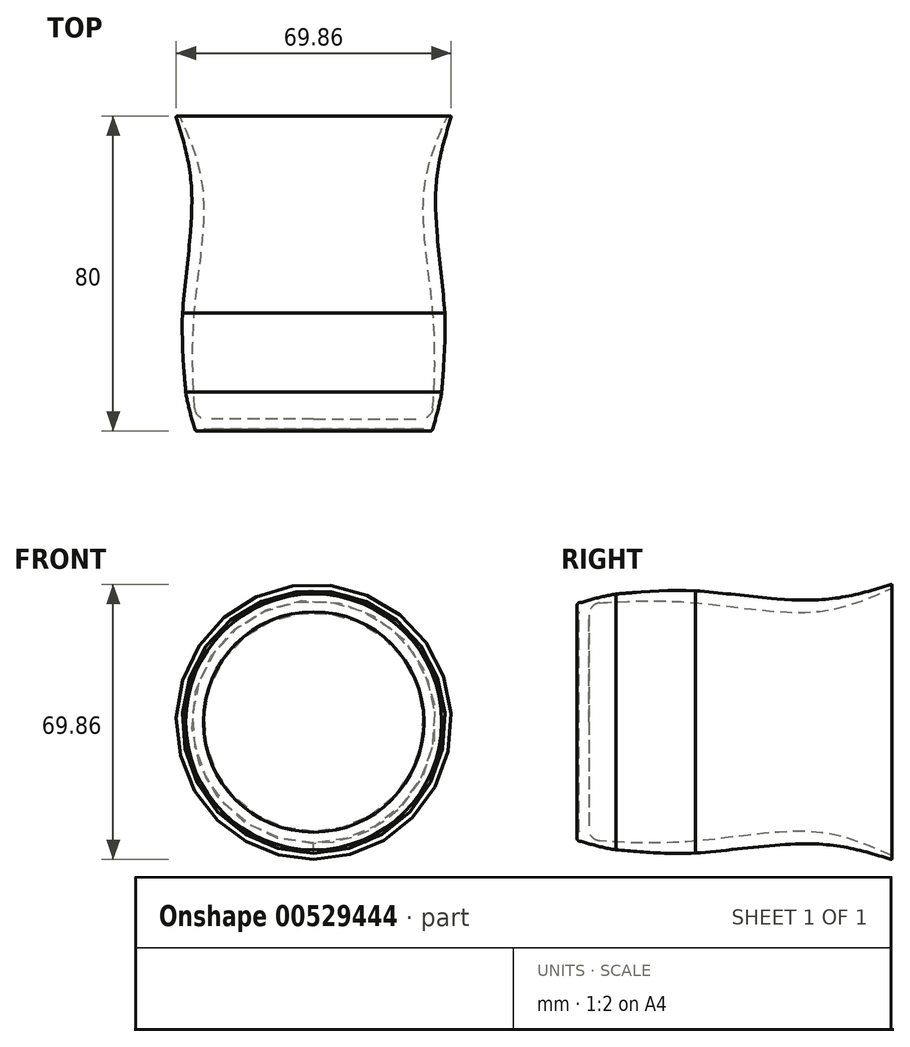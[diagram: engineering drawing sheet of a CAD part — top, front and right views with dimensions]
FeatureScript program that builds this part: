
annotation { "Feature Type Name" : "Feature", "Feature Type Description" : "" }
export const myFeature = defineFeature(function(context is Context, id is Id, definition is map)
    precondition{}
    {
        {
            var Q0;
            Q0=qCreatedBy(makeId("Top.planeOp"),FACE);
            var sketch = newSketch(context, id + "F0", { "sketchPlane" : qUnion([Q0])});
            skLineSegment(sketch, "E0", {"start": v(13.06, 9.6) * mm, "end": v(13.06, 10.1) * mm});
            skLineSegment(sketch, "E1", {"start": v(13.06, 10.1) * mm, "end": v(-14.64, 10.1) * mm});
            skLineSegment(sketch, "E2", {"start": v(-14.94, 9.8) * mm, "end": v(-14.94, 9.8) * mm});
            skLineSegment(sketch, "E3", {"start": v(-15.14, 9.6) * mm, "end": v(-16.64, 9.6) * mm});
            skLineSegment(sketch, "E4", {"start": v(-21.07, 89.6) * mm, "end": v(-21.67, 89.6) * mm});
            skLineSegment(sketch, "E5", {"start": v(-17.01, 9.6) * mm, "end": v(-17.01, 9.6) * mm});
            skLineSegment(sketch, "E6", {"start": v(-19.97, 12.6) * mm, "end": v(-19.94, 12.6) * mm});
            skLineSegment(sketch, "E7", {"start": v(13.06, 10.1) * mm, "end": v(13.06, 12.6) * mm});
            skLineSegment(sketch, "E8", {"start": v(-14.18, 12.6) * mm, "end": v(13.06, 12.6) * mm});
            skLineSegment(sketch, "E9", {"start": v(-21.67, 89.6) * mm, "end": v(-21.07, 89.6) * mm});
            skFitSpline(sketch, "E10", {"points": [v(-20.94, 89.6) * mm, v(-14.94, 70.1) * mm, v(-17.24, 39.63) * mm, v(-17.44, 19.46) * mm, v(-16.94, 12.6) * mm], "startDerivative": vector(30.49, -68.52) * mm, "endDerivative": vector(3.43, -39.56) * mm});
            skPoint(sketch, "E11.visualSharp", {"position": v(-19.94, 9.6) * mm});
            skArc(sketch, "E12.filletArc", {"start": v(-17.17, 15.37) * mm, "mid": v(-16.21, 13.4) * mm, "end": v(-14.18, 12.6) * mm});
            skFitSpline(sketch, "E13", {"points": [v(-18.94, 9.6) * mm, v(-19.44, 19.44) * mm, v(-20.24, 39.6) * mm, v(-17.94, 70.1) * mm, v(-21.94, 89.6) * mm], "startDerivative": vector(-1.88, 51.22) * mm, "endDerivative": vector(-22.07, 71.36) * mm});
            skPoint(sketch, "E14.orphan", {"position": v(-18.04, 9.6) * mm});
            skPoint(sketch, "E15.start.orphan", {"position": v(-17.44, 9.6) * mm});
            skPoint(sketch, "E16.orphan", {"position": v(-19.94, 89.6) * mm});
            skPoint(sketch, "E17.end.orphan", {"position": v(-12.94, 70.1) * mm});
            skArc(sketch, "E18.filletArc", {"start": v(-21.67, 89.6) * mm, "mid": v(-21.83, 89.52) * mm, "end": v(-21.86, 89.34) * mm});
            skArc(sketch, "E19.filletArc", {"start": v(-20.88, 89.48) * mm, "mid": v(-20.96, 89.57) * mm, "end": v(-21.07, 89.6) * mm});
            skPoint(sketch, "E20.visualSharp", {"position": v(-14.94, 9.6) * mm});
            skArc(sketch, "E20.filletArc", {"start": v(-15.14, 9.6) * mm, "mid": v(-15, 9.66) * mm, "end": v(-14.94, 9.8) * mm});
            skPoint(sketch, "E21.visualSharp", {"position": v(-14.94, 10.1) * mm});
            skArc(sketch, "E21.filletArc", {"start": v(-14.64, 10.1) * mm, "mid": v(-14.85, 10.02) * mm, "end": v(-14.94, 9.8) * mm});
            skFitSpline(sketch, "E22", {"points": [v(-17.01, 9.6) * mm, v(-19.44, 19.44) * mm, v(-20.24, 39.6) * mm, v(-17.94, 70.1) * mm, v(-21.94, 89.6) * mm], "startDerivative": vector(-14.91, 50.37) * mm, "endDerivative": vector(-22.12, 71.49) * mm});
            skArc(sketch, "E23.filletArc", {"start": v(-17.12, 9.96) * mm, "mid": v(-16.94, 9.7) * mm, "end": v(-16.64, 9.6) * mm});
            skSolve(sketch);
        }
        {
            var Q0;
            Q0=makeQuery(id+"F0.imprint","IMPRINT",FACE,{"disambiguationData":[TD([[makeQuery(id+"F0.imprint","IMPRINT",EDGE,{"derivedFrom":sQuery(id+"F0.wireOp",EDGE,"E1")}),-1.0]])]});
            var Q1;
            Q1=sQuery(id+"F0.wireOp",EDGE,"E0");
            revolve(context, id + "F1", {"entities" : qUnion([Q0]), "axis" : qUnion([Q1]), "revolveType" : RevolveType.FULL});
        }
    });
